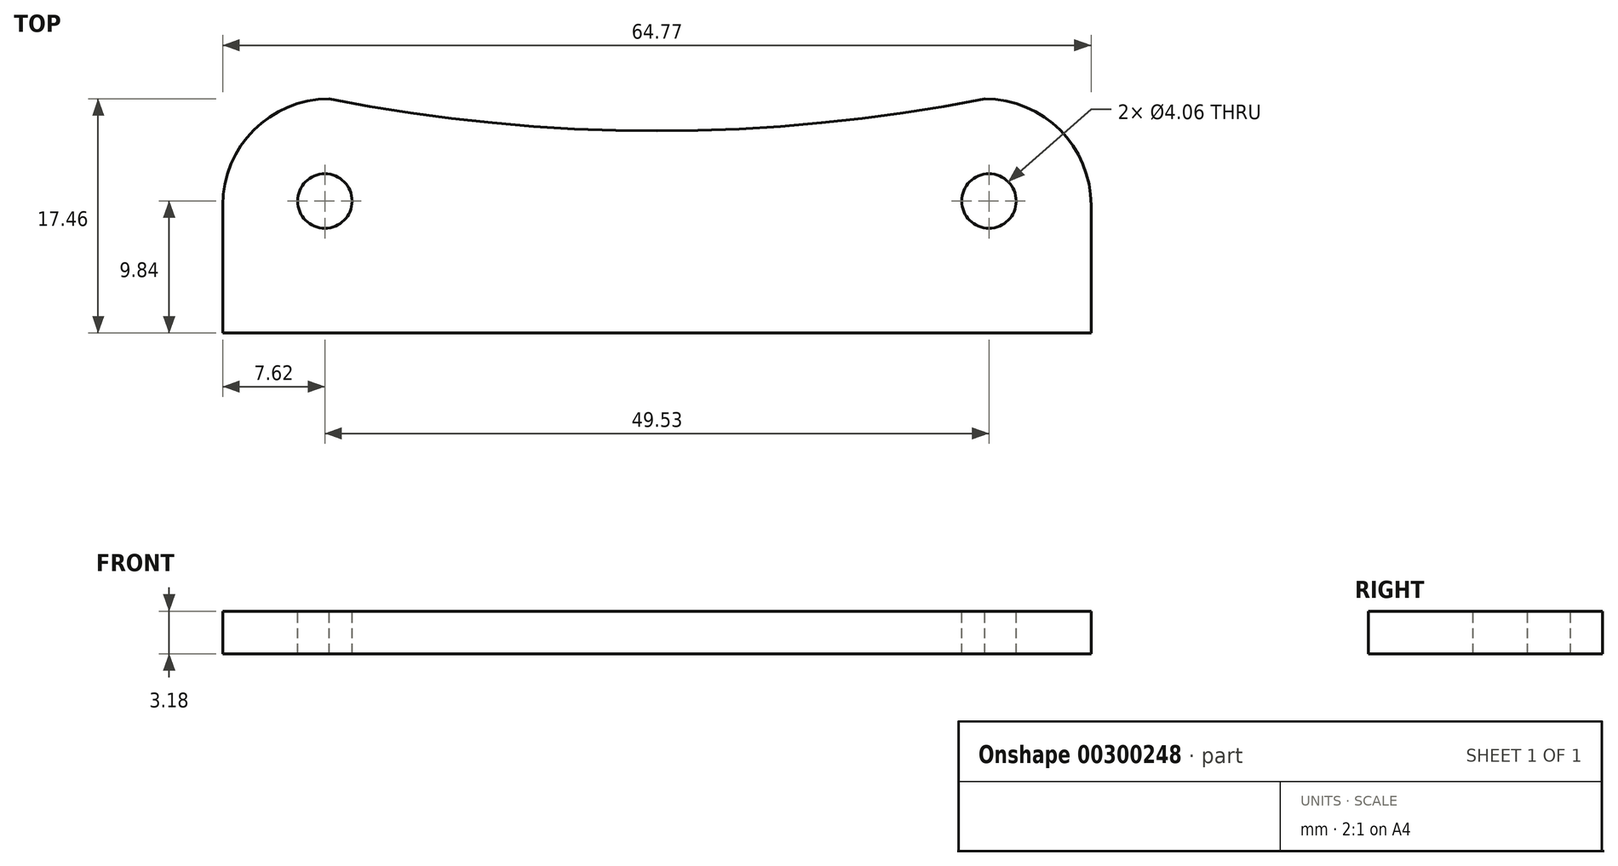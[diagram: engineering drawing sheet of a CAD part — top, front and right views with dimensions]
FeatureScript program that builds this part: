
annotation { "Feature Type Name" : "Feature", "Feature Type Description" : "" }
export const myFeature = defineFeature(function(context is Context, id is Id, definition is map)
    precondition{}
    {
        {
            var Q0;
            Q0=qCreatedBy(makeId("Top.planeOp"),FACE);
            var sketch = newSketch(context, id + "F0", { "sketchPlane" : qUnion([Q0])});
            skLineSegment(sketch, "E0.bottom", {"start": v(7.94, 0) * mm, "end": v(56.83, 0) * mm});
            skLineSegment(sketch, "E0.top", {"start": v(0, -17.46) * mm, "end": v(64.77, -17.46) * mm});
            skLineSegment(sketch, "E0.left", {"start": v(0, -7.94) * mm, "end": v(0, -17.46) * mm});
            skLineSegment(sketch, "E0.right", {"start": v(64.77, -7.94) * mm, "end": v(64.77, -17.46) * mm});
            skCircle(sketch, "E1", {"center": v(7.62, -7.62) * mm, "radius": 2.03 * mm});
            skCircle(sketch, "E2", {"center": v(57.15, -7.62) * mm, "radius": 2.03 * mm});
            skLineSegment(sketch, "E3", {"start": v(32.39, 0) * mm, "end": v(32.39, -17.46) * mm, "construction": true});
            skPoint(sketch, "E4", {"position": v(32.39, -8.73) * mm});
            skLineSegment(sketch, "E5", {"start": v(7.62, -7.62) * mm, "end": v(32.39, -7.62) * mm, "construction": true});
            skLineSegment(sketch, "E6", {"start": v(57.15, -7.62) * mm, "end": v(32.39, -7.62) * mm, "construction": true});
            skPoint(sketch, "E7.visualSharp", {"position": v(0, 0) * mm});
            skArc(sketch, "E7.filletArc", {"start": v(7.94, 0) * mm, "mid": v(2.32, -2.32) * mm, "end": v(0, -7.94) * mm});
            skPoint(sketch, "E8.visualSharp", {"position": v(64.77, 0) * mm});
            skArc(sketch, "E8.filletArc", {"start": v(64.77, -7.94) * mm, "mid": v(62.45, -2.32) * mm, "end": v(56.83, 0) * mm});
            skArc(sketch, "E9", {"start": v(7.94, 0) * mm, "mid": v(32.38, -2.39) * mm, "end": v(56.83, 0) * mm});
            skSolve(sketch);
        }
        {
            var Q0;
            Q0=makeQuery(id+"F0.imprint","IMPRINT",FACE,{"disambiguationData":[TD([[makeQuery(id+"F0.imprint","IMPRINT",EDGE,{"derivedFrom":sQuery(id+"F0.wireOp",EDGE,"E0.top")}),1.0]])]});
            extrude(context, id + "F1", {"entities" : qUnion([Q0]), "oppositeDirection" : true, "depth" : 3.17 * mm});
        }
    });
